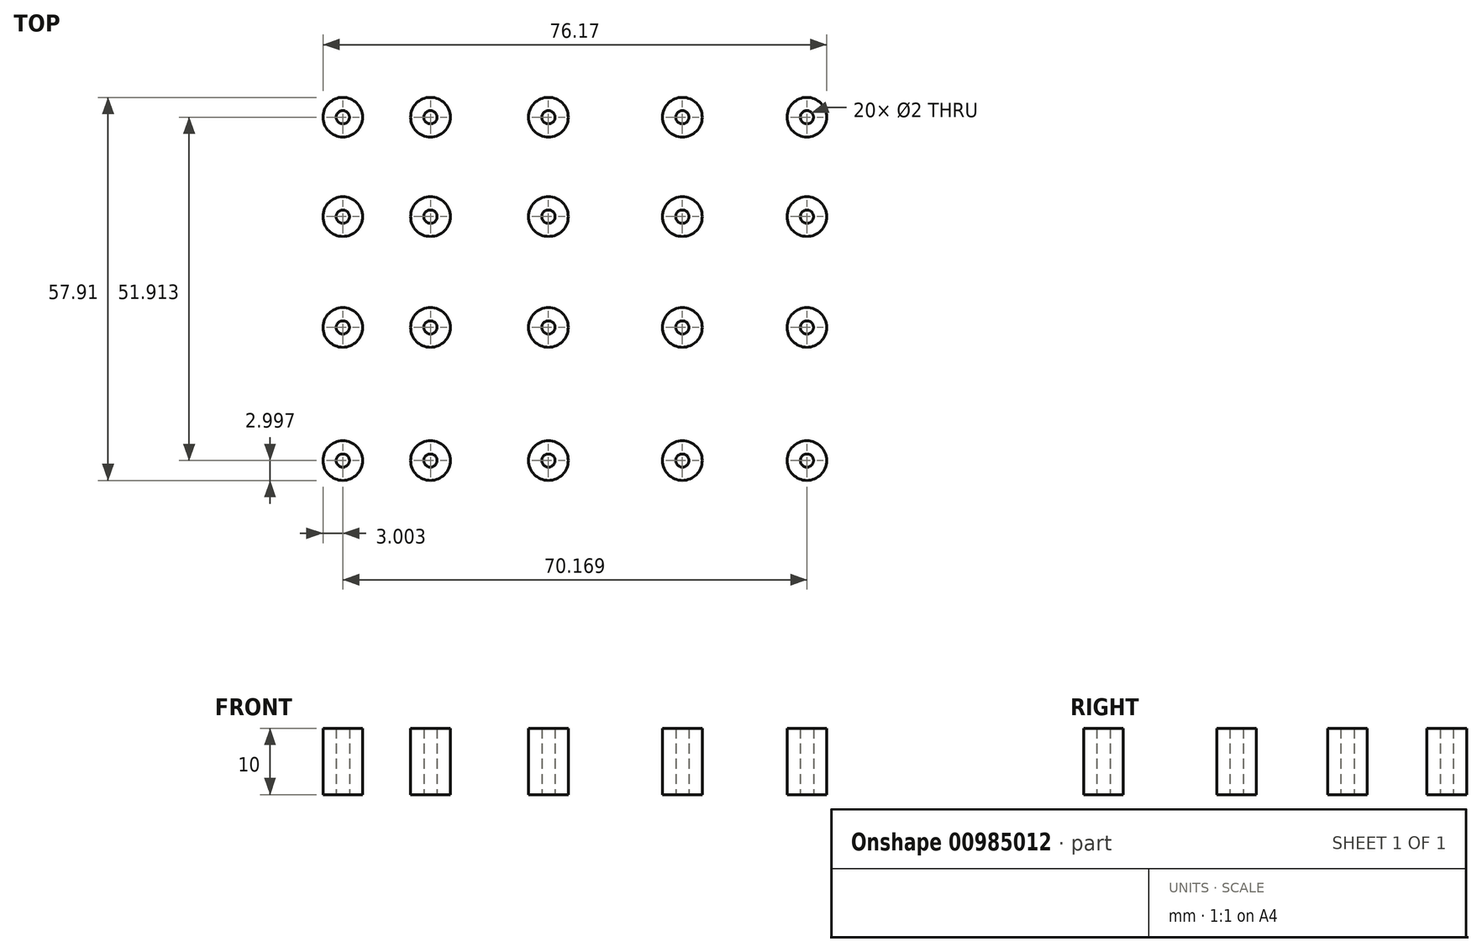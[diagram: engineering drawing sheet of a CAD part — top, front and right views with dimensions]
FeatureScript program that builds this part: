
annotation { "Feature Type Name" : "Feature", "Feature Type Description" : "" }
export const myFeature = defineFeature(function(context is Context, id is Id, definition is map)
    precondition{}
    {
        {
            var Q0;
            Q0=qCreatedBy(makeId("Top.planeOp"),FACE);
            var sketch = newSketch(context, id + "F0", { "sketchPlane" : qUnion([Q0])});
            skCircle(sketch, "E0", {"center": v(-60.68, 45.14) * mm, "radius": 3 * mm});
            skCircle(sketch, "E1", {"center": v(-60.68, 13.36) * mm, "radius": 3 * mm});
            skCircle(sketch, "E2", {"center": v(-47.43, -6.77) * mm, "radius": 3 * mm});
            skCircle(sketch, "E3", {"center": v(-29.6, -6.77) * mm, "radius": 3 * mm});
            skCircle(sketch, "E4", {"center": v(-47.43, 13.36) * mm, "radius": 3 * mm});
            skCircle(sketch, "E5", {"center": v(-29.6, 13.36) * mm, "radius": 3 * mm});
            skCircle(sketch, "E6", {"center": v(-60.68, -6.77) * mm, "radius": 3 * mm});
            skCircle(sketch, "E7", {"center": v(9.5, 30.1) * mm, "radius": 3 * mm});
            skCircle(sketch, "E8", {"center": v(-9.34, 13.36) * mm, "radius": 3 * mm});
            skCircle(sketch, "E9", {"center": v(-9.34, -6.77) * mm, "radius": 3 * mm});
            skCircle(sketch, "E10", {"center": v(9.5, -6.77) * mm, "radius": 3 * mm});
            skCircle(sketch, "E11", {"center": v(-47.43, 30.1) * mm, "radius": 3 * mm});
            skCircle(sketch, "E12", {"center": v(-9.34, 45.14) * mm, "radius": 3 * mm});
            skCircle(sketch, "E13", {"center": v(-29.6, 45.14) * mm, "radius": 3 * mm});
            skCircle(sketch, "E14", {"center": v(-47.43, 45.14) * mm, "radius": 3 * mm});
            skCircle(sketch, "E15", {"center": v(9.5, 45.14) * mm, "radius": 3 * mm});
            skCircle(sketch, "E16", {"center": v(-29.6, 30.1) * mm, "radius": 3 * mm});
            skCircle(sketch, "E17", {"center": v(-9.34, 30.1) * mm, "radius": 3 * mm});
            skCircle(sketch, "E18", {"center": v(9.5, 13.36) * mm, "radius": 3 * mm});
            skCircle(sketch, "E19", {"center": v(-60.68, 30.1) * mm, "radius": 3 * mm});
            skLineSegment(sketch, "E20", {"start": v(-60.68, 45.14) * mm, "end": v(-60.68, -6.77) * mm, "construction": true});
            skLineSegment(sketch, "E21", {"start": v(-47.43, 45.14) * mm, "end": v(-47.43, -6.77) * mm, "construction": true});
            skLineSegment(sketch, "E22", {"start": v(-29.6, 45.14) * mm, "end": v(-29.6, -6.77) * mm, "construction": true});
            skLineSegment(sketch, "E23", {"start": v(-9.34, 45.14) * mm, "end": v(-9.34, -6.77) * mm, "construction": true});
            skLineSegment(sketch, "E24", {"start": v(9.5, 45.14) * mm, "end": v(9.5, -6.77) * mm, "construction": true});
            skSolve(sketch);
        }
        {
            var Q0;
            Q0 = qSketchRegion(id + "F0", true);
            extrude(context, id + "F1", {"entities" : qUnion([Q0]), "depth" : 10 * mm, "offsetDistance" : 25 * mm});
        }
        {
            var Q0;
            Q0=qCreatedBy(makeId("Top.planeOp"),FACE);
            var sketch = newSketch(context, id + "F2", { "sketchPlane" : qUnion([Q0])});
            skCircle(sketch, "E25", {"center": v(-60.68, -6.77) * mm, "radius": 1 * mm});
            skCircle(sketch, "E26", {"center": v(-60.68, 13.36) * mm, "radius": 1 * mm});
            skCircle(sketch, "E27", {"center": v(-60.68, 30.1) * mm, "radius": 1 * mm});
            skCircle(sketch, "E28", {"center": v(-60.68, 45.14) * mm, "radius": 1 * mm});
            skCircle(sketch, "E29", {"center": v(-47.43, 45.14) * mm, "radius": 1 * mm});
            skCircle(sketch, "E30", {"center": v(-47.43, 30.1) * mm, "radius": 1 * mm});
            skCircle(sketch, "E31", {"center": v(-47.43, 13.36) * mm, "radius": 1 * mm});
            skCircle(sketch, "E32", {"center": v(-47.43, -6.77) * mm, "radius": 1 * mm});
            skCircle(sketch, "E33", {"center": v(-29.6, 45.14) * mm, "radius": 1 * mm});
            skCircle(sketch, "E34", {"center": v(-29.6, 30.1) * mm, "radius": 1 * mm});
            skCircle(sketch, "E35", {"center": v(-29.6, 13.36) * mm, "radius": 1 * mm});
            skCircle(sketch, "E36", {"center": v(-29.6, -6.77) * mm, "radius": 1 * mm});
            skCircle(sketch, "E37", {"center": v(-9.34, 45.14) * mm, "radius": 1 * mm});
            skCircle(sketch, "E38", {"center": v(-9.34, 30.1) * mm, "radius": 1 * mm});
            skCircle(sketch, "E39", {"center": v(-9.34, 13.36) * mm, "radius": 1 * mm});
            skCircle(sketch, "E40", {"center": v(-9.34, -6.77) * mm, "radius": 1 * mm});
            skCircle(sketch, "E41", {"center": v(9.5, 45.14) * mm, "radius": 1 * mm});
            skCircle(sketch, "E42", {"center": v(9.5, 30.1) * mm, "radius": 1 * mm});
            skCircle(sketch, "E43", {"center": v(9.5, 13.36) * mm, "radius": 1 * mm});
            skCircle(sketch, "E44", {"center": v(9.5, -6.77) * mm, "radius": 1 * mm});
            skSolve(sketch);
        }
        {
            var Q0;
            Q0 = qSketchRegion(id + "F2", true);
            extrude(context, id + "F3", {"entities" : qUnion([Q0]), "operationType" : NewBodyOperationType.REMOVE, "oppositeDirection" : true, "depth" : -15 * mm, "offsetDistance" : 25 * mm});
        }
    });
